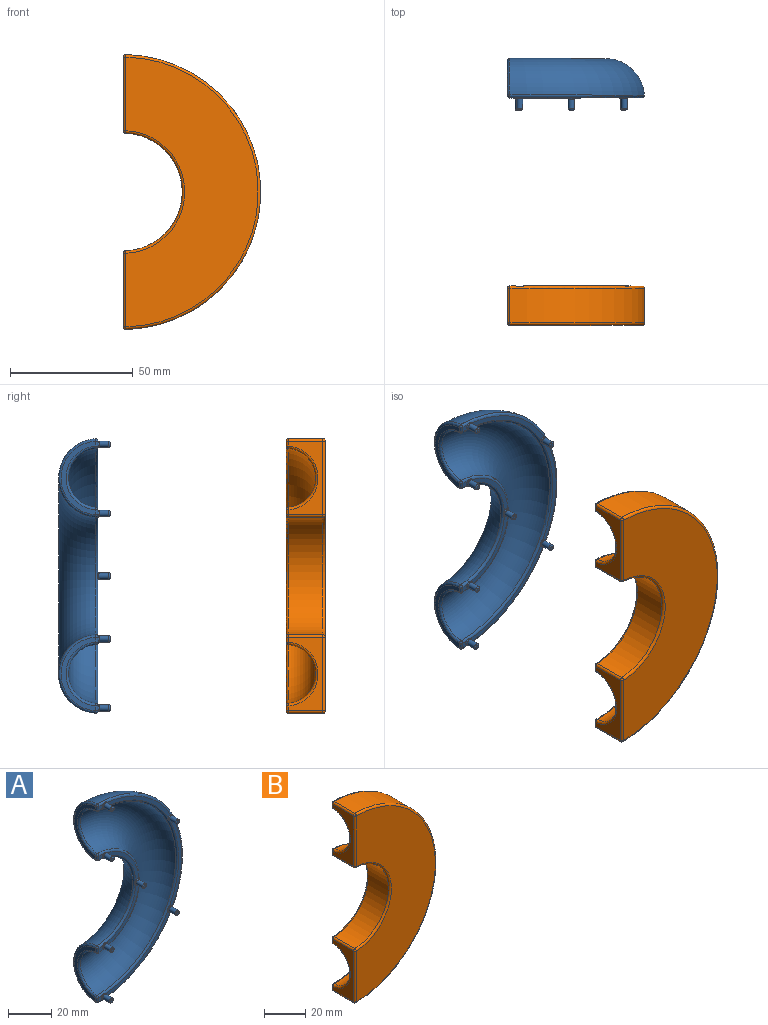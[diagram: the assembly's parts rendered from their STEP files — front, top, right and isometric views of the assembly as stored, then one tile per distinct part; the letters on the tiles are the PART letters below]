
ASSEMBLY  parts=2 mates=2
PART A: 82 faces, bbox 60.6x21x121.2 mm
  f0: plane 24.81x20.82mm, normal (0,-1,0), area 65.3mm2, adj f21,f32,f49,f54
  f1: plane 24.81x20.82mm, normal (0,-1,0), area 65.3mm2, adj f21,f32,f51,f57
  f2: plane 2.75x2.22mm, normal (0,-1,0), area 4.8mm2, adj f21,f29,f32,f48
  f3: plane 41.8x28.04mm, normal (0,-1,0), area 100.4mm2, adj f13,f18,f61,f66
  f4: plane 49.56x7.84mm, normal (0,-1,0), area 100.4mm2, adj f13,f18,f63,f70
  f5: plane 41.52x28.47mm, normal (0,-1,0), area 100.4mm2, adj f13,f18,f67,f73
  f6: plane 2.08x2.02mm, normal (0,-1,0), area 3.5mm2, adj f13,f18,f19,f60
  f7: plane 2.75x2.22mm, normal (0,-1,0), area 4.8mm2, adj f21,f26,f32,f56
  f8: torus R=40mm, axis (0,1,0), area 4433.1mm2, adj f18,f27,f28,f32
  f9: plane 2.62x2.11mm, normal (0,-1,0), area 4.7mm2, adj f13,f17,f18,f72
  f10: torus R=40mm, axis (0,1,0), area 5952.5mm2, adj f13,f16,f20,f21
  f11: plane 29.95x14mm, normal (-1,0,0), area 84mm2, adj f16,f17,f26,f27
  f12: plane 29.95x14mm, normal (-1,0,0), area 84mm2, adj f19,f20,f28,f29
  f13: torus R=54.97mm, axis (0,1,0), area 278.3mm2, adj f3,f4,f5,f6,f9,f10,f14,f15
  f14: sphere r=1mm, area 1.7mm2, adj f13,f16,f17
  f15: sphere r=1mm, area 1.7mm2, adj f13,f19,f20
  f16: bspline ~32.03x15.65mm, area 73.7mm2, adj f10,f11,f14,f22
  f17: cylinder r=1mm len=2.01mm, axis (0,0,-1), area 3.2mm2, adj f9,f11,f14,f23
  f18: torus R=52.96mm, axis (0,1,0), area 238.9mm2, adj f3,f4,f5,f6,f8,f9,f23,f24
  f19: cylinder r=1mm len=2.01mm, axis (0,0,-1), area 3.2mm2, adj f6,f12,f15,f24
  f20: bspline ~32.03x15.65mm, area 73.7mm2, adj f10,f12,f15,f25
  f21: torus R=25.03mm, axis (0,-1,0), area 119.2mm2, adj f0,f1,f2,f7,f10,f22,f25,f47
  f22: sphere r=1mm, area 1.6mm2, adj f16,f21,f26
  f23: sphere r=1mm, area 1.5mm2, adj f17,f18,f27
  f24: sphere r=1mm, area 1.5mm2, adj f18,f19,f28
  f25: sphere r=1mm, area 1.6mm2, adj f20,f21,f29
  f26: cylinder r=1mm len=2.01mm, axis (0,0,-1), area 3.2mm2, adj f7,f11,f22,f30
  f27: bspline ~26.01x12.72mm, area 58.2mm2, adj f8,f11,f23,f30
  f28: bspline ~26.01x12.72mm, area 58.2mm2, adj f8,f12,f24,f31
  f29: cylinder r=1mm len=2.01mm, axis (0,0,-1), area 3.2mm2, adj f2,f12,f25,f31
  f30: sphere r=1mm, area 1.5mm2, adj f26,f27,f32
  f31: sphere r=1mm, area 1.5mm2, adj f28,f29,f32
  f32: torus R=27.04mm, axis (0,-1,0), area 123.6mm2, adj f0,f1,f2,f7,f8,f30,f31,f50
  f33: cylinder r=1.25mm len=4.22mm, axis (0,1,0), area 31.9mm2, adj f71,f72,f73,f74,f81
  f34: plane 1.5x1.5mm, normal (0,-1,0), area 1.8mm2, adj f81
  f35: cylinder r=1.25mm len=4.22mm, axis (0,1,0), area 31.9mm2, adj f67,f68,f69,f70,f80
  f36: plane 1.5x1.5mm, normal (0,-1,0), area 1.8mm2, adj f80
  f37: cylinder r=1.25mm len=4.22mm, axis (0,1,0), area 31.9mm2, adj f63,f64,f65,f66,f79
  f38: plane 1.5x1.5mm, normal (0,-1,0), area 1.8mm2, adj f79
  f39: cylinder r=1.25mm len=4.22mm, axis (0,1,0), area 31.9mm2, adj f59,f60,f61,f62,f78
  f40: plane 1.5x1.5mm, normal (0,-1,0), area 1.8mm2, adj f78
  f41: cylinder r=1.25mm len=4.2mm, axis (0,1,0), area 31.9mm2, adj f55,f56,f57,f58,f77
  f42: plane 1.5x1.5mm, normal (0,-1,0), area 1.8mm2, adj f77
  f43: cylinder r=1.25mm len=4.2mm, axis (0,1,0), area 31.9mm2, adj f51,f52,f53,f54,f76
  f44: plane 1.5x1.5mm, normal (0,-1,0), area 1.8mm2, adj f76
  f45: cylinder r=1.25mm len=4.2mm, axis (0,1,0), area 31.9mm2, adj f47,f48,f49,f50,f75
  f46: plane 1.5x1.5mm, normal (0,-1,0), area 1.8mm2, adj f75
  f47: bspline ~3.04x1.17mm, area 1.6mm2, adj f21,f45,f48,f49
  f48: torus R=1.75mm, axis (0,1,0), area 1.4mm2, adj f2,f45,f47,f50
  f49: torus R=1.75mm, axis (0,1,0), area 1.4mm2, adj f0,f45,f47,f50
  f50: bspline ~3.14x1.24mm, area 1.7mm2, adj f32,f45,f48,f49
  f51: torus R=1.75mm, axis (0,1,0), area 1.4mm2, adj f1,f43,f52,f53
  f52: bspline ~3.1x0.92mm, area 1.6mm2, adj f21,f43,f51,f54
  f53: bspline ~3.1x0.99mm, area 1.7mm2, adj f32,f43,f51,f54
  f54: torus R=1.75mm, axis (0,1,0), area 1.4mm2, adj f0,f43,f52,f53
  f55: bspline ~3.14x1.24mm, area 1.7mm2, adj f32,f41,f56,f57
  f56: torus R=1.75mm, axis (0,1,0), area 1.4mm2, adj f7,f41,f55,f58
  f57: torus R=1.75mm, axis (0,1,0), area 1.4mm2, adj f1,f41,f55,f58
  f58: bspline ~3.04x1.17mm, area 1.6mm2, adj f21,f41,f56,f57
  f59: bspline ~2.98x0.89mm, area 1.6mm2, adj f18,f39,f60,f61
  f60: torus R=1.75mm, axis (0,1,0), area 1.4mm2, adj f6,f39,f59,f62
  f61: torus R=1.75mm, axis (0,1,0), area 1.4mm2, adj f3,f39,f59,f62
  f62: bspline ~3.12x0.95mm, area 1.7mm2, adj f13,f39,f60,f61
  f63: torus R=1.75mm, axis (0,1,0), area 1.4mm2, adj f4,f37,f64,f65
  f64: bspline ~2.71x1.65mm, area 1.6mm2, adj f18,f37,f63,f66
  f65: bspline ~2.82x1.71mm, area 1.7mm2, adj f13,f37,f63,f66
  f66: torus R=1.75mm, axis (0,1,0), area 1.4mm2, adj f3,f37,f64,f65
  f67: torus R=1.75mm, axis (0,1,0), area 1.4mm2, adj f5,f35,f68,f69
  f68: bspline ~2.73x1.63mm, area 1.6mm2, adj f18,f35,f67,f70
  f69: bspline ~2.84x1.69mm, area 1.7mm2, adj f13,f35,f67,f70
  f70: torus R=1.75mm, axis (0,1,0), area 1.4mm2, adj f4,f35,f68,f69
  f71: bspline ~3.2x1.1mm, area 1.7mm2, adj f13,f33,f72,f73
  f72: torus R=1.75mm, axis (0,1,0), area 1.4mm2, adj f9,f33,f71,f74
  f73: torus R=1.75mm, axis (0,1,0), area 1.4mm2, adj f5,f33,f71,f74
  f74: bspline ~3.07x1.04mm, area 1.6mm2, adj f18,f33,f72,f73
  f75: torus R=0.75mm, axis (0,-1,0), area 5.3mm2, adj f45,f46
  f76: torus R=0.75mm, axis (0,-1,0), area 5.3mm2, adj f43,f44
  f77: torus R=0.75mm, axis (0,-1,0), area 5.3mm2, adj f41,f42
  f78: torus R=0.75mm, axis (0,-1,0), area 5.3mm2, adj f39,f40
  f79: torus R=0.75mm, axis (0,-1,0), area 5.3mm2, adj f37,f38
  f80: torus R=0.75mm, axis (0,-1,0), area 5.3mm2, adj f35,f36
  f81: torus R=0.75mm, axis (0,-1,0), area 5.3mm2, adj f33,f34
PART B: 73 faces, bbox 60.6x16x121.2 mm
  f0: plane 23.88x20.06mm, normal (0,1,0), area 63.6mm2, adj f31,f37,f38,f44
  f1: plane 23.88x20.06mm, normal (0,1,0), area 63.6mm2, adj f31,f36,f37,f44
  f2: plane 2.17x2.02mm, normal (0,1,0), area 3.5mm2, adj f31,f38,f44,f45
  f3: plane 2.1x1.9mm, normal (0,1,0), area 3.4mm2, adj f52,f60,f63,f64
  f4: plane 40.45x27.76mm, normal (0,1,0), area 99.4mm2, adj f58,f60,f63,f64
  f5: plane 48.29x7.53mm, normal (0,1,0), area 99.4mm2, adj f57,f58,f63,f64
  f6: plane 40.71x27.34mm, normal (0,1,0), area 99.4mm2, adj f57,f63,f64,f65
  f7: plane 2.17x2.02mm, normal (0,1,0), area 3.5mm2, adj f31,f36,f43,f44
  f8: plane 2.07x1.3mm, normal (0,1,0), area 2.2mm2, adj f55,f63,f64,f65
  f9: plane 30.01x14mm, normal (-1,0,0), area 180.6mm2, adj f30,f42,f43,f51,f52,f53
  f10: plane 30.01x14mm, normal (-1,0,0), area 180.6mm2, adj f32,f40,f45,f50,f54,f55
  f11: plane 109.98x54mm, normal (0,-1,0), area 3709.9mm2, adj f29,f40,f41,f42
  f12: cylinder r=56mm len=111.98mm, axis (0,-1,0), area 2434.5mm2, adj f41,f50,f51,f63
  f13: cylinder r=24mm len=47.96mm, axis (0,-1,0), area 1028.7mm2, adj f29,f30,f31,f32
  f14: torus R=40mm, axis (0,-1,0), area 4428.1mm2, adj f44,f53,f54,f64
  f15: cylinder r=1.4mm len=4mm, axis (0,1,0), area 35.2mm2, adj f65,f66
  f16: plane 0.8x0.8mm, normal (0,1,0), area 0.5mm2, adj f66
  f17: cylinder r=1.4mm len=4mm, axis (0,1,0), area 35.2mm2, adj f57,f67
  f18: plane 0.8x0.8mm, normal (0,1,0), area 0.5mm2, adj f67
  f19: cylinder r=1.4mm len=4mm, axis (0,1,0), area 35.2mm2, adj f58,f68
  f20: plane 0.8x0.8mm, normal (0,1,0), area 0.5mm2, adj f68
  f21: cylinder r=1.4mm len=4mm, axis (0,1,0), area 35.2mm2, adj f60,f69
  f22: plane 0.8x0.8mm, normal (0,1,0), area 0.5mm2, adj f69
  f23: cylinder r=1.4mm len=4mm, axis (0,1,0), area 35.2mm2, adj f36,f72
  f24: plane 0.8x0.8mm, normal (0,1,0), area 0.5mm2, adj f72
  f25: cylinder r=1.4mm len=4mm, axis (0,1,0), area 35.2mm2, adj f38,f70
  f26: plane 0.8x0.8mm, normal (0,1,0), area 0.5mm2, adj f70
  f27: cylinder r=1.4mm len=4mm, axis (0,1,0), area 35.2mm2, adj f37,f71
  f28: plane 0.8x0.8mm, normal (0,1,0), area 0.5mm2, adj f71
  f29: torus R=25mm, axis (0,-1,0), area 117.2mm2, adj f11,f13,f33,f34
  f30: cylinder r=1mm len=14mm, axis (0,-1,0), area 21.4mm2, adj f9,f13,f34,f35
  f31: torus R=25mm, axis (0,1,0), area 110.9mm2, adj f0,f1,f2,f7,f13,f35,f36,f37
  f32: cylinder r=1mm len=14mm, axis (0,-1,0), area 21.4mm2, adj f10,f13,f33,f39
  f33: sphere r=1mm, area 1.5mm2, adj f29,f32,f40
  f34: sphere r=1mm, area 1.5mm2, adj f29,f30,f42
  f35: sphere r=1mm, area 1.5mm2, adj f30,f31,f43
  f36: torus R=2.4mm, axis (0,1,0), area 12.7mm2, adj f1,f7,f23,f31,f44
  f37: torus R=2.4mm, axis (0,1,0), area 12.5mm2, adj f0,f1,f27,f31,f44
  f38: torus R=2.4mm, axis (0,1,0), area 12.7mm2, adj f0,f2,f25,f31,f44
  f39: sphere r=1mm, area 1.5mm2, adj f31,f32,f45
  f40: cylinder r=1mm len=30.01mm, axis (0,0,1), area 47.1mm2, adj f10,f11,f33,f46
  f41: torus R=55mm, axis (0,-1,0), area 271.4mm2, adj f11,f12,f46,f47
  f42: cylinder r=1mm len=30.01mm, axis (0,0,-1), area 47.1mm2, adj f9,f11,f34,f47
  f43: cylinder r=1mm len=2.04mm, axis (0,0,1), area 3.2mm2, adj f7,f9,f35,f48
  f44: torus R=27.04mm, axis (0,-1,0), area 120.4mm2, adj f0,f1,f2,f7,f14,f36,f37,f38
  f45: cylinder r=1mm len=2.04mm, axis (0,0,1), area 3.2mm2, adj f2,f10,f39,f49
  f46: sphere r=1mm, area 1.6mm2, adj f40,f41,f50
  f47: sphere r=1mm, area 1.6mm2, adj f41,f42,f51
  f48: sphere r=1mm, area 1.7mm2, adj f43,f44,f53
  f49: sphere r=1mm, area 1.7mm2, adj f44,f45,f54
  f50: cylinder r=1mm len=14mm, axis (0,-1,0), area 22.2mm2, adj f10,f12,f46,f56
  f51: cylinder r=1mm len=14mm, axis (0,-1,0), area 22.2mm2, adj f9,f12,f47,f59
  f52: cylinder r=1mm len=2.04mm, axis (0,0,1), area 3.2mm2, adj f3,f9,f59,f61
  f53: bspline ~26.01x12.72mm, area 58.2mm2, adj f9,f14,f48,f61
  f54: bspline ~26.01x12.72mm, area 58.2mm2, adj f10,f14,f49,f62
  f55: cylinder r=1mm len=2.04mm, axis (0,0,1), area 3.2mm2, adj f8,f10,f56,f62
  f56: sphere r=1mm, area 1.6mm2, adj f50,f55,f63
  f57: torus R=2.4mm, axis (0,1,0), area 12.5mm2, adj f5,f6,f17,f63,f64
  f58: torus R=2.4mm, axis (0,1,0), area 12.5mm2, adj f4,f5,f19,f63,f64
  f59: sphere r=1mm, area 1.6mm2, adj f51,f52,f63
  f60: torus R=2.4mm, axis (0,1,0), area 12.7mm2, adj f3,f4,f21,f63,f64
  f61: sphere r=1mm, area 1.4mm2, adj f52,f53,f64
  f62: sphere r=1mm, area 1.4mm2, adj f54,f55,f64
  f63: torus R=55mm, axis (0,1,0), area 262.6mm2, adj f3,f4,f5,f6,f8,f12,f56,f57
  f64: torus R=52.96mm, axis (0,1,0), area 234.4mm2, adj f3,f4,f5,f6,f8,f14,f57,f58
  f65: torus R=2.4mm, axis (0,1,0), area 12.7mm2, adj f6,f8,f15,f63,f64
  f66: torus R=0.4mm, axis (0,1,0), area 10.2mm2, adj f15,f16
  f67: torus R=0.4mm, axis (0,1,0), area 10.2mm2, adj f17,f18
  f68: torus R=0.4mm, axis (0,1,0), area 10.2mm2, adj f19,f20
  f69: torus R=0.4mm, axis (0,1,0), area 10.2mm2, adj f21,f22
  f70: torus R=0.4mm, axis (0,1,0), area 10.2mm2, adj f25,f26
  f71: torus R=0.4mm, axis (0,1,0), area 10.2mm2, adj f27,f28
  f72: torus R=0.4mm, axis (0,1,0), area 10.2mm2, adj f23,f24
PLACE A t=(-22.39,69.91,-16.67)mm
PLACE B t=(-22.39,-6.88,-16.67)mm fixed
MATE slider A.f39 <-> B.f15  axis (0,1,0) through (-17.97,65.41,-70.49)mm
MATE slider A.f33 <-> B.f21  axis (0,1,0) through (-17.39,67.53,37.09)mm
